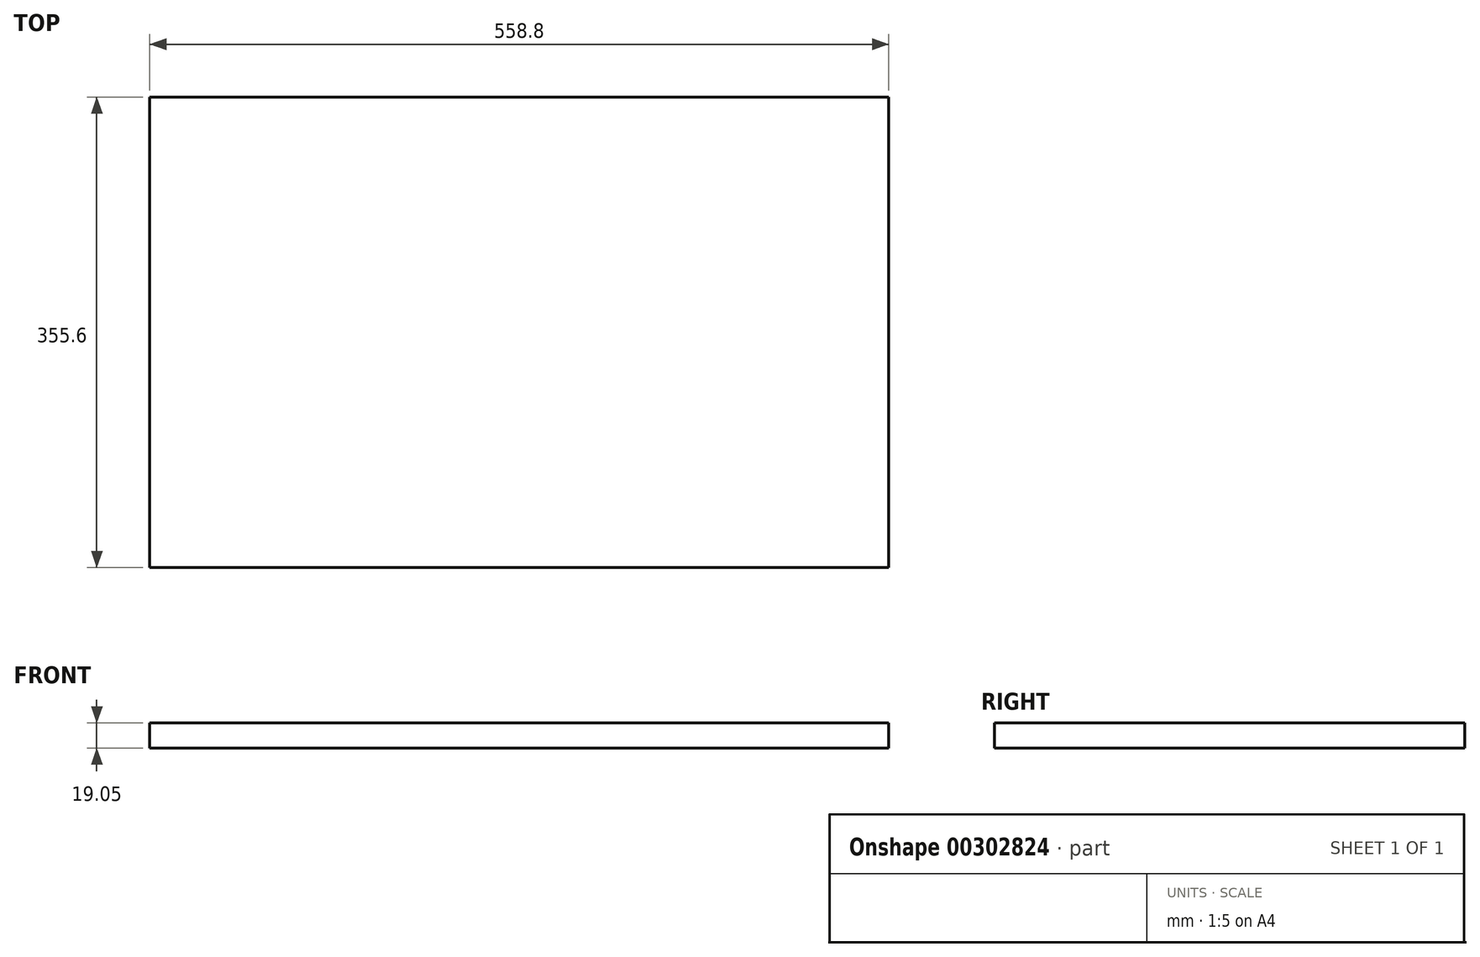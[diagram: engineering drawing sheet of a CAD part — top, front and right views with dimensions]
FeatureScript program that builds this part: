
annotation { "Feature Type Name" : "Feature", "Feature Type Description" : "" }
export const myFeature = defineFeature(function(context is Context, id is Id, definition is map)
    precondition{}
    {
        {
            var Q0;
            Q0=qCreatedBy(makeId("Top.planeOp"),FACE);
            var sketch = newSketch(context, id + "F0", { "sketchPlane" : qUnion([Q0])});
            skLineSegment(sketch, "E0.bottom", {"start": v(-279.4, 177.8) * mm, "end": v(279.4, 177.8) * mm});
            skLineSegment(sketch, "E0.top", {"start": v(-279.4, -177.8) * mm, "end": v(279.4, -177.8) * mm});
            skLineSegment(sketch, "E0.left", {"start": v(-279.4, 177.8) * mm, "end": v(-279.4, -177.8) * mm});
            skLineSegment(sketch, "E0.right", {"start": v(279.4, 177.8) * mm, "end": v(279.4, -177.8) * mm});
            skSolve(sketch);
        }
        {
            var Q0;
            Q0=makeQuery(id+"F0.imprint","IMPRINT",FACE,{"disambiguationData":[TD([[makeQuery(id+"F0.imprint","IMPRINT",EDGE,{"derivedFrom":sQuery(id+"F0.wireOp",EDGE,"E0.bottom")}),-1.0]])]});
            extrude(context, id + "F1", {"entities" : qUnion([Q0]), "depth" : 19.05 * mm});
        }
    });
